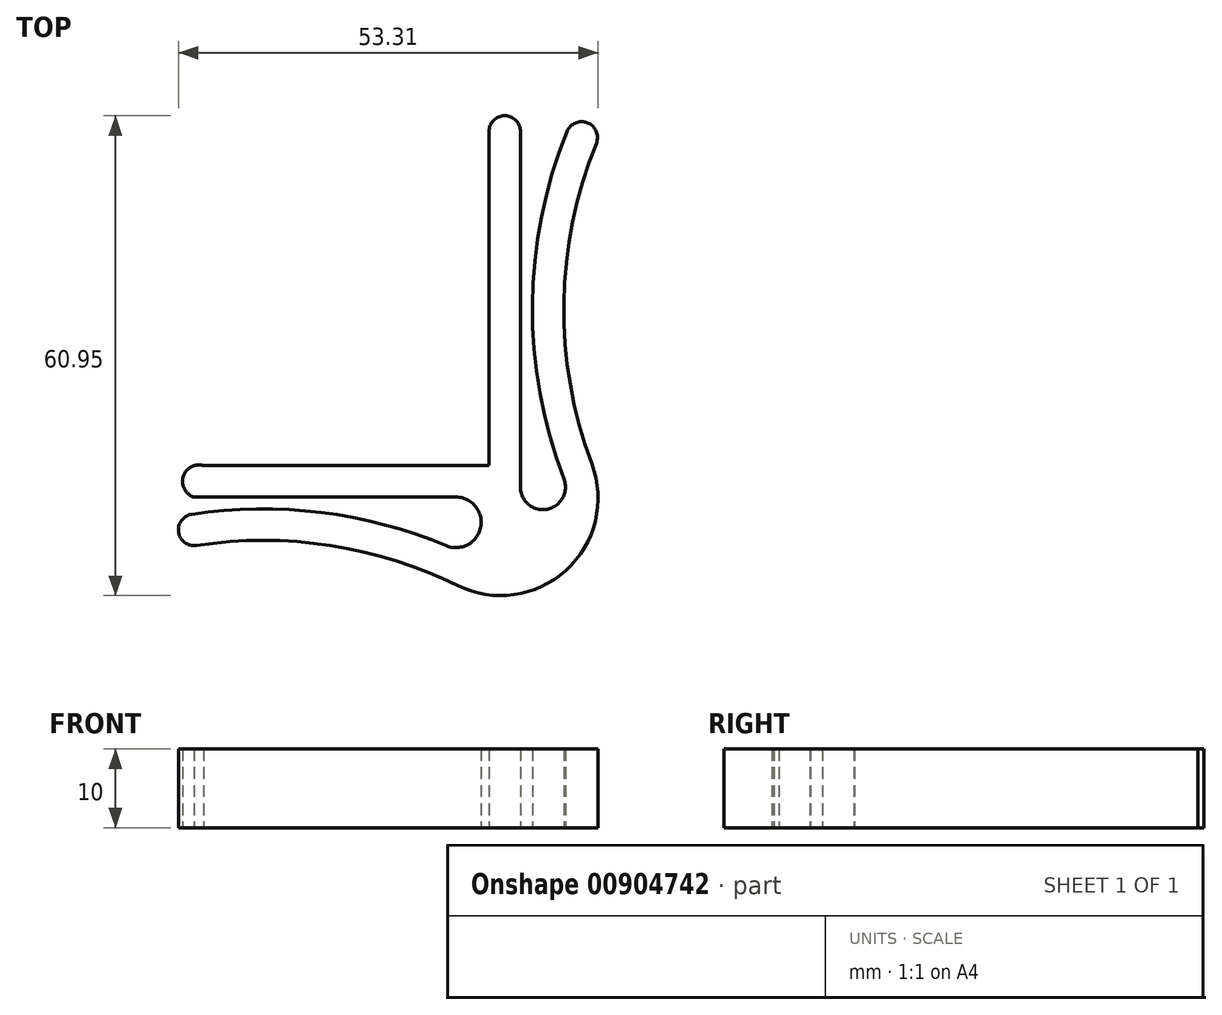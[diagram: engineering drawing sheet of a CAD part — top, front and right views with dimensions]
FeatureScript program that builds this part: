
annotation { "Feature Type Name" : "Feature", "Feature Type Description" : "" }
export const myFeature = defineFeature(function(context is Context, id is Id, definition is map)
    precondition{}
    {
        {
            var Q0;
            Q0=qCreatedBy(makeId("Top.planeOp"),FACE);
            var sketch = newSketch(context, id + "F0", { "sketchPlane" : qUnion([Q0])});
            skLineSegment(sketch, "E0", {"start": v(0, -21.86) * mm, "end": v(0, 9.37) * mm});
            skLineSegment(sketch, "E1", {"start": v(0, 9.37) * mm, "end": v(4, 9.37) * mm, "construction": true});
            skLineSegment(sketch, "E2", {"start": v(4, 9.37) * mm, "end": v(4, -35.82) * mm});
            skArc(sketch, "E3", {"start": v(9.92, 9.37) * mm, "mid": v(5.5, -12.67) * mm, "end": v(9.51, -34.8) * mm});
            skPoint(sketch, "E4", {"position": v(4, -13.22) * mm});
            skArc(sketch, "E5.0", {"start": v(13.62, 7.86) * mm, "mid": v(9.5, -12.45) * mm, "end": v(13.06, -32.87) * mm});
            skPoint(sketch, "E6", {"position": v(9.92, 9.37) * mm});
            skArc(sketch, "E7", {"start": v(13.62, 7.86) * mm, "mid": v(12.52, 10.47) * mm, "end": v(9.92, 9.37) * mm});
            skArc(sketch, "E8", {"start": v(4, 9.37) * mm, "mid": v(2, 11.37) * mm, "end": v(0, 9.37) * mm});
            skPoint(sketch, "E9", {"position": v(8.13, -35.82) * mm});
            skPoint(sketch, "E10.orphan", {"position": v(9.51, -12.06) * mm});
            skLineSegment(sketch, "E11", {"start": v(-7.77, -33.08) * mm, "end": v(-36.23, -33.08) * mm});
            skArc(sketch, "E12", {"start": v(-36.23, -33.08) * mm, "mid": v(-38.85, -34.46) * mm, "end": v(-37.46, -37.08) * mm});
            skArc(sketch, "E13", {"start": v(-5.46, -43.25) * mm, "mid": v(-21.34, -39.03) * mm, "end": v(-37.77, -39.27) * mm});
            skArc(sketch, "E14.0", {"start": v(-3.98, -48.31) * mm, "mid": v(-20.18, -43.22) * mm, "end": v(-37.16, -43.22) * mm});
            skPoint(sketch, "E15", {"position": v(-28.67, -38.58) * mm});
            skArc(sketch, "E16", {"start": v(-37.77, -39.27) * mm, "mid": v(-39.44, -41.55) * mm, "end": v(-37.16, -43.22) * mm});
            skPoint(sketch, "E17", {"position": v(-3.98, -48.31) * mm});
            skArc(sketch, "E18", {"start": v(13.06, -32.87) * mm, "mid": v(9.78, -46.38) * mm, "end": v(-3.98, -48.31) * mm});
            skArc(sketch, "E19", {"start": v(-5.46, -43.25) * mm, "mid": v(-1.06, -40.92) * mm, "end": v(-4.21, -37.08) * mm});
            skLineSegment(sketch, "E20", {"start": v(-37.46, -37.08) * mm, "end": v(-4.21, -37.08) * mm});
            skLineSegment(sketch, "E21", {"start": v(0, -21.86) * mm, "end": v(0, -33.08) * mm});
            skLineSegment(sketch, "E22", {"start": v(0, -33.08) * mm, "end": v(-7.77, -33.08) * mm});
            skArc(sketch, "E23", {"start": v(4, -35.82) * mm, "mid": v(7.37, -38.62) * mm, "end": v(9.51, -34.8) * mm});
            skSolve(sketch);
        }
        {
            var Q0;
            Q0 = qSketchRegion(id + "F0", true);
            extrude(context, id + "F1", {"entities" : qUnion([Q0]), "depth" : 10 * mm, "offsetDistance" : 25 * mm});
        }
    });
